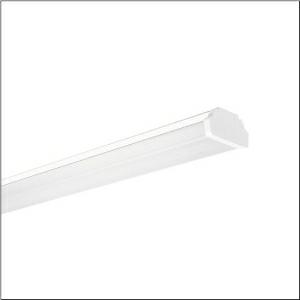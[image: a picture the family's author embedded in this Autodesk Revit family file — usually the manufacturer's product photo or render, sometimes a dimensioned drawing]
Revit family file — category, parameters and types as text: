
# Revit family: dus_r__31_gen_2_53bd8127v68xc2_f58f
name_source: partatom
category: Lighting Fixtures
units: mm (PartAtom-declared; Revit-internal decimal feet)

## family parameters
Cut with Voids When Loaded = No
Host = Face
Light Source = No
Part Type = Normal
Room Calculation Point = No
Round Connector Dimension = Use Diameter
Shared = No

## types (1)
- DUS® 31 Gen.2 (1 x LED, 8340 lm, 47.9 W, 6500K)
    Apparent Load = 48 VA
    CIE Flux Codes = 47 80 95 93 100
    Color Rendering = 80
    Color Temperature = 6500K
    Default Elevation = 1800 mm
    Description = DUS® 31 Gen.2, luminaire insert, of sheet steel, coil coated, white, length: 1.535mm, width: 81mm, height: 90mm, 5x system unit, system units: 307mm, LED rated luminous flux: 8.340lm, light colour: 865, control gear: ON/OFF, control gear: ECG, with plug, 3-pole, with phase selection, mains connection: 220..240V, AC, 50/60Hz, rated input power: 48W, through-wiring accessed according to module size, primary optical cover: cover, of PMMA, light emission: direct distribution, primary light characteristic: symmetric, protection rating (complete): IP20, protection rating (LED compartment): IP50, insulation class (complete): insulation class I (protective earthing), certification: CE, ENEC, VDE, UKCA, impact resistance: IK03, permissible ambient temperature for indoor applications: -35..+45°C, corresponds to IFS (International Featured Standards) requirements for safety and quality in the food industry, reducing of maximum allowable ambient temperature of 5°C with ceiling mounting, packaging unit: 1 piece
    Height = 95 mm
    Lamp = 1 x LED
    Lamp Light Flux = 8340 lm
    Lamp Power = 47.9 W
    Lamp count = 1
    Length = 1535 mm
    Luminous efficacy = 174 lm/W
    Manufacturer = Siteco
    ModVariant = No
    Model = 53BD8127V68XC2
    Mounting Place = Ceiling
    Mounting Type = Pendant
    Number of Poles = 1
    OnlyDefault = Yes
    Power Factor = 1
    Product Name = DUS® 31 Gen.2
    Product group = luminaire insert | ceiling pendant
    ProductGroupID = 902
    Protection Class = Protection class I
    Protection Degree = IP 20
    RLX_Detail_Level = 1
    RLX_Emergency_Light_Flux = 0 lm
    RLX_Emergency_Type = 0
    RLX_Emergency_Type_DB = No
    RlxData = <blob elided: 28453 chars, md5=5a090f60>
    Socket = socket
    Standby Power = 0 W
    System Light Flux = 8340 lm
    System Power = 48 W
    Type Comments = Product without accessories
    Type Image = l_1319596.jpg
    URL = http://relux.com
    VarID = ---
    Voltage = 0 V
    Weight = 0.00 kg
    Width = 81 mm

## geometry (parser evidence)
native form markers: Blend x4, Sweep x13
no freeform markers — native parametric forms only
